# Revit family: R62 - Generic
name_source: partatom
category: Puertas
revit_build: Autodesk Revit 2014 (Build: 20130308_1515(x64)
units: mm (PartAtom-declared; Revit-internal decimal feet)

## types (6) — shared parameters
AccessibilityPerformance = 4-6/min.
AccessoryOptions = contact manufacturer
AntiFingerTrapRequirement = No
BIMObjectName = agtatec_Record_SldngDrset_R62 SecurityDoor_WallBased
Capacity = 4-6/min.
Category = Security gate/portal
Colour = Aluminium
Descripción = Circular sliding door
DoorNumber = 2
DoorsetOperation = automatic
DrumWallPanelFill = agtatec_Record_Revolving Door, Laminated Safety Glass (Clear)
DurationUnit = Year
ElectronicLock = Sí
Features = Separation, anti-tailgating, anti-piggybacking
Finish = Powder coated, Anodized, customer specific
FireExit = No
Flooring = agtatec_Record_Revolving Door, Felt Carpet
FrameFinishOptions = Stainless steel and more
FrameMaterial = Aluminium
FrameProfile = Aluminium
Función = Exterior
GlassLayers = 2
GlassThickness1 = 2438.4 mm
GlassThickness2 = 3048 mm
GlassType = part of glazing spec
HasDrive = Sí
IfcExportAs = IFCDoorStyle
IfcExportType = Door
IsExternal = Sí
LeafColourOptions = all RAL, customer specific
LeafPanelFill = agtatec_Record_Revolving Door, Laminated Safety Glass (Clear)
ManufacturerName = record
ManufacturerURL = www.agta-record.com
Material = Aluminium
ModelReference = depends on the configuration
Modelo = R62
NBSDescription = Sliding Doorset
NBSReference = 25-50-20/175
Name = SldngDrset_R62-SecurityDoor_Generic_Record
NominalHeight = 640080 mm
OpenEntry = No
OpenExit = No
OpeningAngleEntry = 45.00°
OpeningAngleExit = 45.00°
Operación = automatic
PanelFrames = agtatec_Record_Revolving Door, Aluminium
ProductInformation = www.agta-record.com
ReplacementCost = Depends on the configuration and door type
SafetyDevices = Optical sensors
SelfClosing = Sí
Shape = Cylinder Shaped
Size = XxxXXxXX
SmokeStop = No
ThresholdRequired = No
Tipo de construcción = Automatic Revolving Door
URL = www.agta-record.com
Uniclass2 = Ss_25_30_20_77
Version = 1
WarrantyDescription = Depends on country
WarrantyDurationLabour = Depends on country
WarrantyDurationParts = Depends on country
WarrantyDurationUnit = Depends on country
WarrantyGuarantorLabour = Local door manufacturer
WarrantyGuarantorParts = Local door manufacturer
WithinStandardSizes = Sí
zero-valued in all types: Costo, GlazingAreaFraction, ThermalTransmittance

## per-type parameters (varying)
- Record R62 600 - Single: Altura=2420 mm; Altura aproximada=2426 mm; Anchura=1060 mm; Anchura aproximada=1197.3 mm; CanopyHeight=220 mm  [stored 0.721785 ft]; CanopyRadius=520.5 mm; Clasificación para incendios=x; Comentarios de tipo=x; DiameterOptions=1035mm, 1090mm depends on glas type; DocumentReference=x; Documentation=x; Floor Frame (Ring)=No; FrameSeal=No; HandicapAccessible=No; InnerGlassRadius=461 mm; InnerRadius=456 mm; InsideDiameter=912 mm; IssueDate=x; LateralRadius1=513.05 mm; LateralRadius2=516.05 mm; MethodOfMeasurement=x; ModelLabel=x; NominalLength=315468 mm; NominalWidth=315468 mm; Nota clave=x; OuterGlassRadius=471 mm; OuterRadius=517.5 mm; OutsideDiameter=1035 mm; PassageHeight=2200 mm; PassageWidth=441.6 mm  [stored 1.44882 ft]; PassageWidthOptions=600; Process=x; ProductionYear=x; RecessHeight=2470 mm; RecessWidth=1243.2 mm; ReferenceStandard=x; ServiceLifeDuration=x; ServiceLifeType=x; TotalDiameter=1143.2 mm; TotalHeight=2420 mm; Weight=ca. 355-475kg
- Record R62 900 - Double: Altura=3210 mm; Altura aproximada=3216 mm; Anchura=1535 mm; Anchura aproximada=1672.3 mm; CanopyHeight=610 mm  [stored 2.00131 ft]; CanopyRadius=758 mm  [stored 2.48688 ft]; DiameterOptions=1455mm, 1510mm depends on glas type; Floor Frame (Ring)=Sí; FrameSeal=Sí; HandicapAccessible=Sí; InnerGlassRadius=698.5 mm  [stored 2.29167 ft]; InnerRadius=693.5 mm  [stored 2.27526 ft]; InsideDiameter=1387 mm; IssueDate=<>; LateralRadius1=750.55 mm; LateralRadius2=753.55 mm; NominalLength=443484 mm; NominalWidth=443484 mm; OuterGlassRadius=708.5 mm  [stored 2.32448 ft]; OuterRadius=755 mm  [stored 2.47703 ft]; OutsideDiameter=1510 mm; PassageHeight=2600 mm; PassageWidth=679.1 mm  [stored 2.22802 ft]; PassageWidthOptions=900; RecessHeight=3260 mm; RecessWidth=1718.2 mm; ReferenceStandard=EN16005, EN16361, DIN 18650, etc.; ServiceLifeDuration=10-15 years; TotalDiameter=1618.2 mm; TotalHeight=3210 mm; Weight=ca. 460-640kg
- Record R62 1100 - Double: Altura=4000 mm; Altura aproximada=4006 mm; Anchura=1815 mm; Anchura aproximada=1952.3 mm; CanopyHeight=1000 mm; CanopyRadius=898 mm; DiameterOptions=1735mm, 1790mm depends on glas type; Floor Frame (Ring)=Sí; FrameSeal=Sí; HandicapAccessible=Sí; InnerGlassRadius=838.5 mm; InnerRadius=833.5 mm  [stored 2.73458 ft]; InsideDiameter=1667 mm; LateralRadius1=890.55 mm; LateralRadius2=893.55 mm; NominalLength=528828 mm; NominalWidth=528828 mm; OuterGlassRadius=848.5 mm; OuterRadius=895 mm; OutsideDiameter=1790 mm; PassageHeight=3000 mm; PassageWidth=819.1 mm  [stored 2.68734 ft]; PassageWidthOptions=1100; RecessHeight=4050 mm; RecessWidth=1998.2 mm; ReferenceStandard=EN16005, EN16361, DIN 18650, etc.; ServiceLifeDuration=10-15 years; TotalDiameter=1898.2 mm; TotalHeight=4000 mm; Weight=ca. 538-760kg
- Record R62 600 - Double: Altura=2420 mm; Altura aproximada=2426 mm; Anchura=1115 mm; Anchura aproximada=1252.3 mm; CanopyHeight=220 mm  [stored 0.721785 ft]; CanopyRadius=548 mm  [stored 1.7979 ft]; Clasificación para incendios=x; Comentarios de tipo=x; DiameterOptions=1035mm, 1090mm depends on glas type; DocumentReference=x; Documentation=x; Floor Frame (Ring)=No; FrameSeal=No; HandicapAccessible=No; InnerGlassRadius=488.5 mm; InnerRadius=483.5 mm; InsideDiameter=967 mm; IssueDate=x; LateralRadius1=540.55 mm; LateralRadius2=543.55 mm; MethodOfMeasurement=x; ModelLabel=x; NominalLength=315468 mm; NominalWidth=315468 mm; Nota clave=x; OuterGlassRadius=498.5 mm; OuterRadius=545 mm  [stored 1.78806 ft]; OutsideDiameter=1090 mm; PassageHeight=2200 mm; PassageWidth=469.1 mm  [stored 1.53904 ft]; PassageWidthOptions=600; Process=x; ProductionYear=x; RecessHeight=2470 mm; RecessWidth=1298.2 mm; ReferenceStandard=x; ServiceLifeDuration=x; ServiceLifeType=x; TotalDiameter=1198.2 mm; TotalHeight=2420 mm; Weight=ca. 355-475kg
- Record R62 900 - Single: Altura=3210 mm; Altura aproximada=3216 mm; Anchura=1480 mm; Anchura aproximada=1617.3 mm; CanopyHeight=610 mm  [stored 2.00131 ft]; CanopyRadius=730.5 mm  [stored 2.39665 ft]; DiameterOptions=1455mm, 1510mm depends on glas type; Floor Frame (Ring)=Sí; FrameSeal=Sí; HandicapAccessible=Sí; InnerGlassRadius=671 mm  [stored 2.20144 ft]; InnerRadius=666 mm  [stored 2.18504 ft]; InsideDiameter=1332 mm; IssueDate=<>; LateralRadius1=723.05 mm; LateralRadius2=726.05 mm; NominalLength=443484 mm; NominalWidth=443484 mm; OuterGlassRadius=681 mm  [stored 2.23425 ft]; OuterRadius=727.5 mm  [stored 2.38681 ft]; OutsideDiameter=1455 mm; PassageHeight=2600 mm; PassageWidth=651.6 mm  [stored 2.1378 ft]; PassageWidthOptions=900; RecessHeight=3260 mm; RecessWidth=1663.2 mm; ReferenceStandard=EN16005, EN16361, DIN 18650, etc.; ServiceLifeDuration=10-15 years; TotalDiameter=1563.2 mm; TotalHeight=3210 mm; Weight=ca. 460-640kg
- Record R62 1100 - Single: Altura=4000 mm; Altura aproximada=4006 mm; Anchura=1760 mm; Anchura aproximada=1897.3 mm; CanopyHeight=1000 mm; CanopyRadius=870.5 mm; DiameterOptions=1735mm, 1790mm depends on glas type; Floor Frame (Ring)=Sí; FrameSeal=Sí; HandicapAccessible=Sí; InnerGlassRadius=811 mm  [stored 2.66076 ft]; InnerRadius=806 mm  [stored 2.64436 ft]; InsideDiameter=1612 mm; LateralRadius1=863.05 mm; LateralRadius2=866.05 mm; NominalLength=528828 mm; NominalWidth=528828 mm; OuterGlassRadius=821 mm  [stored 2.69357 ft]; OuterRadius=867.5 mm; OutsideDiameter=1735 mm; PassageHeight=3000 mm; PassageWidth=791.6 mm  [stored 2.59711 ft]; PassageWidthOptions=1100; RecessHeight=4050 mm; RecessWidth=1943.2 mm; ReferenceStandard=EN16005, EN16361, DIN 18650, etc.; ServiceLifeDuration=10-15 years; TotalDiameter=1843.2 mm; TotalHeight=4000 mm; Weight=ca. 538-760kg

note: [stored X ft] marks values corroborated as IEEE doubles in the binary element streams (Revit-internal decimal feet)

## geometry (parser evidence)
native form markers: Blend x4, Sweep x5
no freeform markers — native parametric forms only
